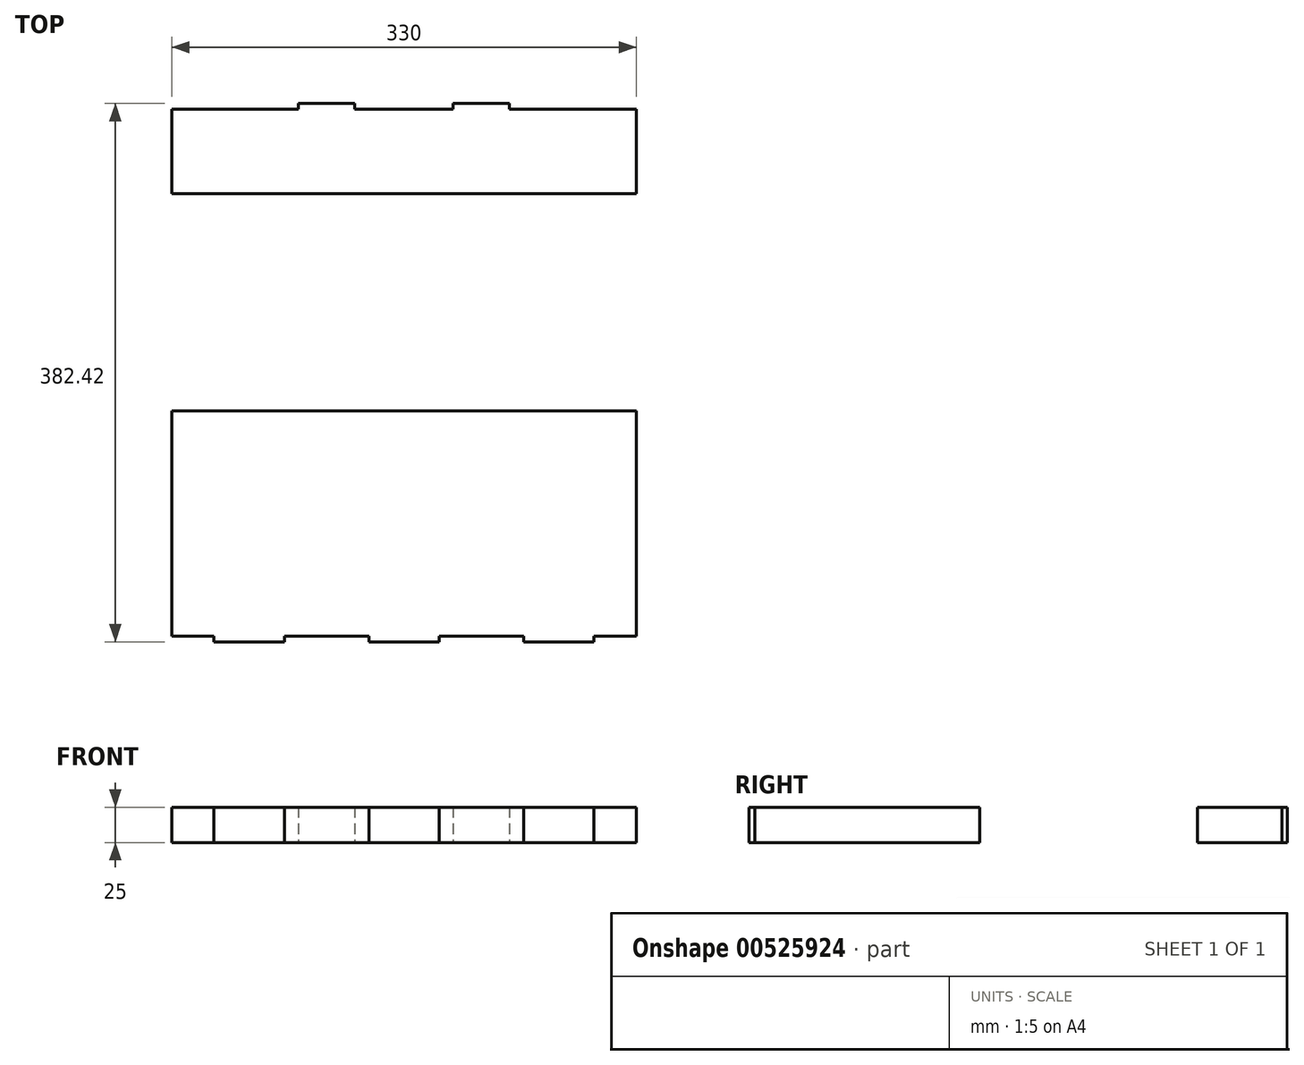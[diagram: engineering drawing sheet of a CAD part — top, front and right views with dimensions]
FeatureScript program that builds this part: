
annotation { "Feature Type Name" : "Feature", "Feature Type Description" : "" }
export const myFeature = defineFeature(function(context is Context, id is Id, definition is map)
    precondition{}
    {
        {
            var Q0;
            Q0=qCreatedBy(makeId("Top.planeOp"),FACE);
            var sketch = newSketch(context, id + "F0", { "sketchPlane" : qUnion([Q0])});
            skLineSegment(sketch, "E0.bottom", {"start": v(165, -30) * mm, "end": v(-165, -30) * mm});
            skLineSegment(sketch, "E0.top", {"start": v(165, 30) * mm, "end": v(-165, 30) * mm});
            skLineSegment(sketch, "E0.left", {"start": v(165, -30) * mm, "end": v(165, 30) * mm});
            skLineSegment(sketch, "E0.right", {"start": v(-165, -30) * mm, "end": v(-165, 30) * mm});
            skPoint(sketch, "E0.middle", {"position": v(0, 0) * mm});
            skSolve(sketch);
        }
        {
            var Q0;
            Q0=makeQuery(id+"F0.imprint","IMPRINT",FACE,{"disambiguationData":[TD([[makeQuery(id+"F0.imprint","IMPRINT",EDGE,{"derivedFrom":sQuery(id+"F0.wireOp",EDGE,"E0.bottom")}),-1.0]])]});
            extrude(context, id + "F1", {"entities" : qUnion([Q0]), "depth" : 25 * mm, "offsetDistance" : 25 * mm});
        }
        {
            var Q0;
            Q0=makeQuery(id+"F1.opExtrude","SWEPT_FACE",FACE,{"disambiguationData":[OSD([sQuery(id+"F0.wireOp",EDGE,"E0.top")])]});
            var sketch = newSketch(context, id + "F2", { "sketchPlane" : qUnion([Q0])});
            skLineSegment(sketch, "E1.bottom", {"start": v(-75, 25) * mm, "end": v(-35, 25) * mm});
            skLineSegment(sketch, "E1.top", {"start": v(-75, 0) * mm, "end": v(-35, 0) * mm});
            skLineSegment(sketch, "E1.left", {"start": v(-75, 25) * mm, "end": v(-75, 0) * mm});
            skLineSegment(sketch, "E1.right", {"start": v(-35, 25) * mm, "end": v(-35, 0) * mm});
            skLineSegment(sketch, "E2.bottom", {"start": v(35, 25) * mm, "end": v(75, 25) * mm});
            skLineSegment(sketch, "E2.top", {"start": v(35, 0) * mm, "end": v(75, 0) * mm});
            skLineSegment(sketch, "E2.left", {"start": v(35, 25) * mm, "end": v(35, 0) * mm});
            skLineSegment(sketch, "E2.right", {"start": v(75, 25) * mm, "end": v(75, 0) * mm});
            skSolve(sketch);
        }
        {
            var Q0;
            Q0 = qSketchRegion(id + "F2", true);
            extrude(context, id + "F3", {"entities" : qUnion([Q0]), "operationType" : NewBodyOperationType.ADD, "depth" : 4 * mm, "offsetDistance" : 25 * mm});
        }
        {
            var Q0;
            Q0=qCreatedBy(makeId("Top.planeOp"),FACE);
            var sketch = newSketch(context, id + "F4", { "sketchPlane" : qUnion([Q0])});
            skLineSegment(sketch, "E3.bottom", {"start": v(165, -184.42) * mm, "end": v(-165, -184.42) * mm});
            skLineSegment(sketch, "E3.top", {"start": v(165, -344.42) * mm, "end": v(-165, -344.42) * mm});
            skLineSegment(sketch, "E3.left", {"start": v(165, -184.42) * mm, "end": v(165, -344.42) * mm});
            skLineSegment(sketch, "E3.right", {"start": v(-165, -184.42) * mm, "end": v(-165, -344.42) * mm});
            skPoint(sketch, "E3.middle", {"position": v(0, -264.42) * mm});
            skSolve(sketch);
        }
        {
            var Q0;
            Q0 = qSketchRegion(id + "F4", true);
            extrude(context, id + "F5", {"entities" : qUnion([Q0]), "depth" : 25 * mm, "offsetDistance" : 25 * mm});
        }
        {
            var Q0;
            Q0=makeQuery(id+"F5.opExtrude","SWEPT_FACE",FACE,{"disambiguationData":[OSD([sQuery(id+"F4.wireOp",EDGE,"E3.top")])]});
            var sketch = newSketch(context, id + "F6", { "sketchPlane" : qUnion([Q0])});
            skLineSegment(sketch, "E4.bottom", {"start": v(-135, 25) * mm, "end": v(-85, 25) * mm});
            skLineSegment(sketch, "E4.top", {"start": v(-135, 0) * mm, "end": v(-85, 0) * mm});
            skLineSegment(sketch, "E4.left", {"start": v(-135, 25) * mm, "end": v(-135, 0) * mm});
            skLineSegment(sketch, "E4.right", {"start": v(-85, 25) * mm, "end": v(-85, 0) * mm});
            skLineSegment(sketch, "E5.bottom", {"start": v(85, 25) * mm, "end": v(135, 25) * mm});
            skLineSegment(sketch, "E5.top", {"start": v(85, 0) * mm, "end": v(135, 0) * mm});
            skLineSegment(sketch, "E5.left", {"start": v(85, 25) * mm, "end": v(85, 0) * mm});
            skLineSegment(sketch, "E5.right", {"start": v(135, 25) * mm, "end": v(135, 0) * mm});
            skLineSegment(sketch, "E6.bottom", {"start": v(-25, 25) * mm, "end": v(25, 25) * mm});
            skLineSegment(sketch, "E6.top", {"start": v(-25, 0) * mm, "end": v(25, 0) * mm});
            skLineSegment(sketch, "E6.left", {"start": v(-25, 25) * mm, "end": v(-25, 0) * mm});
            skLineSegment(sketch, "E6.right", {"start": v(25, 25) * mm, "end": v(25, 0) * mm});
            skSolve(sketch);
        }
        {
            var Q0;
            Q0 = qSketchRegion(id + "F6", true);
            extrude(context, id + "F7", {"entities" : qUnion([Q0]), "operationType" : NewBodyOperationType.ADD, "depth" : 4 * mm, "offsetDistance" : 25 * mm});
        }
    });
